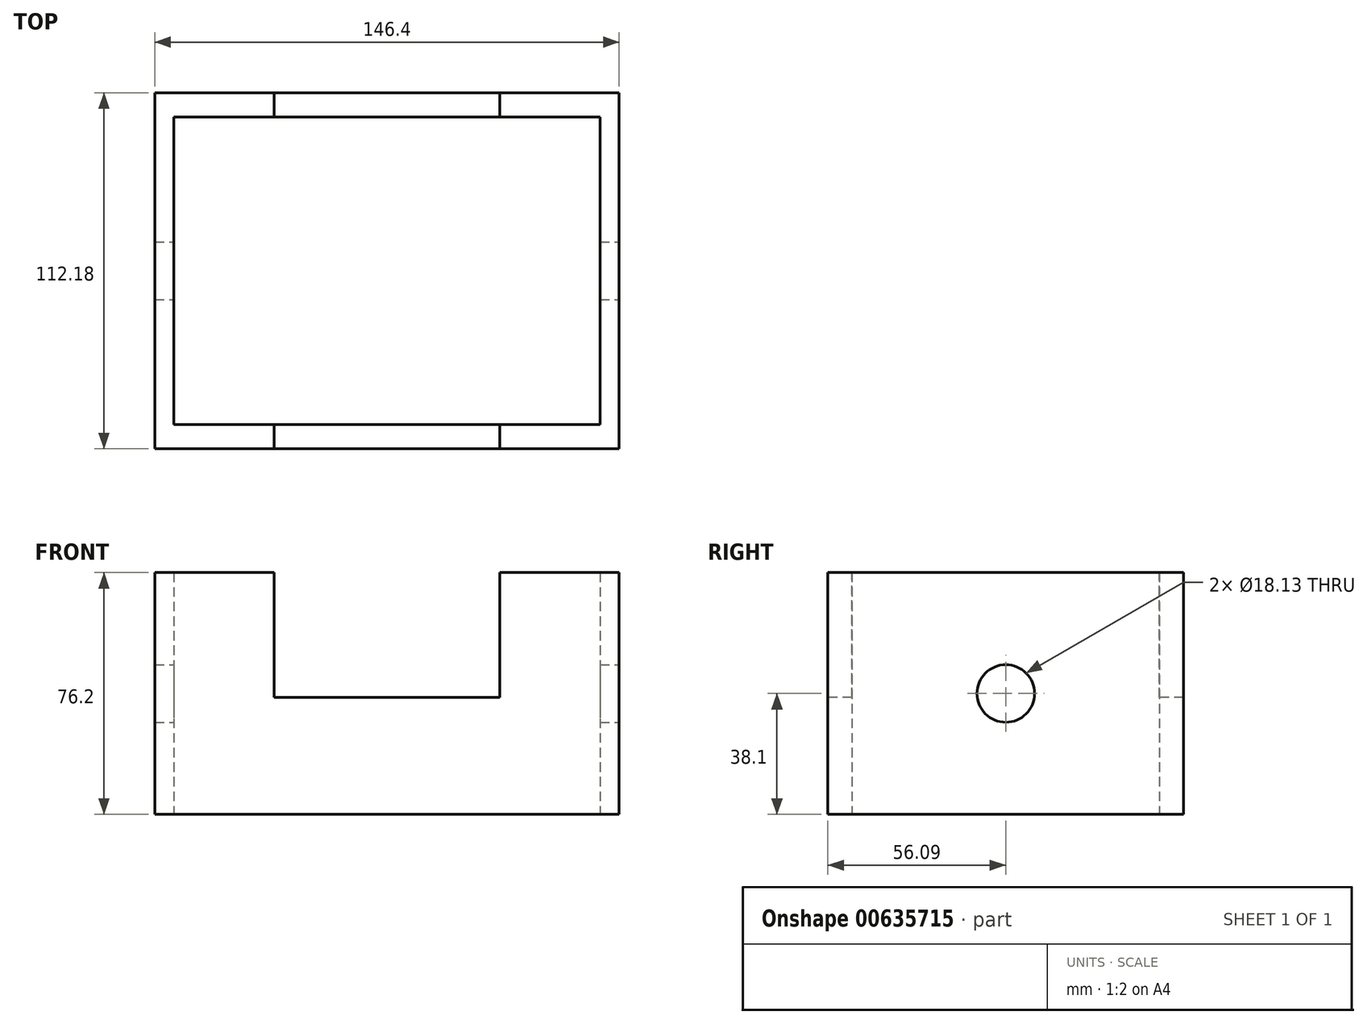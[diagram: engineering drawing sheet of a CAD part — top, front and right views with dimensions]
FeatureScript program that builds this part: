
annotation { "Feature Type Name" : "Feature", "Feature Type Description" : "" }
export const myFeature = defineFeature(function(context is Context, id is Id, definition is map)
    precondition{}
    {
        {
            var Q0;
            Q0=qCreatedBy(makeId("Top.planeOp"),FACE);
            var sketch = newSketch(context, id + "F0", { "sketchPlane" : qUnion([Q0])});
            skLineSegment(sketch, "E0.bottom", {"start": v(73.2, -56.1) * mm, "end": v(-73.2, -56.1) * mm});
            skLineSegment(sketch, "E0.top", {"start": v(73.2, 56.1) * mm, "end": v(-73.2, 56.1) * mm});
            skLineSegment(sketch, "E0.left", {"start": v(73.2, -56.1) * mm, "end": v(73.2, 56.1) * mm});
            skLineSegment(sketch, "E0.right", {"start": v(-73.2, -56.1) * mm, "end": v(-73.2, 56.1) * mm});
            skPoint(sketch, "E0.middle", {"position": v(0, 0) * mm});
            skLineSegment(sketch, "E1.bottom", {"start": v(67.15, -48.44) * mm, "end": v(-67.15, -48.44) * mm});
            skLineSegment(sketch, "E1.top", {"start": v(67.15, 48.44) * mm, "end": v(-67.15, 48.44) * mm});
            skLineSegment(sketch, "E1.left", {"start": v(67.15, -48.44) * mm, "end": v(67.15, 48.44) * mm});
            skLineSegment(sketch, "E1.right", {"start": v(-67.15, -48.44) * mm, "end": v(-67.15, 48.44) * mm});
            skSolve(sketch);
        }
        {
            var Q0;
            Q0=makeQuery(id+"F0.imprint","IMPRINT",FACE,{"disambiguationData":[TD([[makeQuery(id+"F0.imprint","IMPRINT",EDGE,{"derivedFrom":sQuery(id+"F0.wireOp",EDGE,"E0.bottom")}),-1.0]])]});
            extrude(context, id + "F1", {"entities" : qUnion([Q0]), "depth" : 76.2 * mm, "offsetDistance" : 25.4 * mm});
        }
        {
            var Q0;
            Q0=makeQuery(id+"F1.opExtrude","SWEPT_FACE",FACE,{"disambiguationData":[OSD([sQuery(id+"F0.wireOp",EDGE,"E0.bottom")])]});
            var sketch = newSketch(context, id + "F2", { "sketchPlane" : qUnion([Q0])});
            skLineSegment(sketch, "E2.bottom", {"start": v(35.5, 36.91) * mm, "end": v(-35.5, 36.91) * mm});
            skLineSegment(sketch, "E2.top", {"start": v(35.5, 115.49) * mm, "end": v(-35.5, 115.49) * mm});
            skLineSegment(sketch, "E2.left", {"start": v(35.5, 36.91) * mm, "end": v(35.5, 115.49) * mm});
            skLineSegment(sketch, "E2.right", {"start": v(-35.5, 36.91) * mm, "end": v(-35.5, 115.49) * mm});
            skPoint(sketch, "E2.middle", {"position": v(0, 76.2) * mm});
            skSolve(sketch);
        }
        {
            var Q0;
            {var subQ0=sQuery(id+"F2.wireOp",EDGE,"E2.top");Q0=makeQuery(id+"F2.imprint","IMPRINT",FACE,{"disambiguationData":[TD([[makeQuery(id+"F2.imprint","IMPRINT",EDGE,{"derivedFrom":subQ0}),1.0]])]});}
            var Q1;
            {var subQ0=sQuery(id+"F2.wireOp",EDGE,"E2.bottom");Q1=makeQuery(id+"F2.imprint","IMPRINT",FACE,{"disambiguationData":[TD([[makeQuery(id+"F2.imprint","IMPRINT",EDGE,{"derivedFrom":subQ0}),-1.0]])]});}
            extrude(context, id + "F3", {"entities" : qUnion([Q0, Q1]), "operationType" : NewBodyOperationType.REMOVE, "endBound" : BoundingType.THROUGH_ALL, "oppositeDirection" : true, "depth" : 25.4 * mm, "offsetDistance" : 25.4 * mm});
        }
        {
            var Q0;
            Q0=makeQuery(id+"F1.opExtrude","SWEPT_FACE",FACE,{"disambiguationData":[OSD([sQuery(id+"F0.wireOp",EDGE,"E0.left")])]});
            var sketch = newSketch(context, id + "F4", { "sketchPlane" : qUnion([Q0])});
            skCircle(sketch, "E3", {"center": v(0, 38.1) * mm, "radius": 9.07 * mm});
            skPoint(sketch, "E3.centerSnap0", {"position": v(56.1, 38.1) * mm});
            skPoint(sketch, "E3.centerSnap1", {"position": v(0, 76.2) * mm});
            skSolve(sketch);
        }
        {
            var Q0;
            Q0=makeQuery(id+"F4.imprint","IMPRINT",FACE,{"disambiguationData":[TD([[makeQuery(id+"F4.imprint","IMPRINT",EDGE,{"derivedFrom":sQuery(id+"F4.wireOp",EDGE,"E3")}),1.0]])]});
            extrude(context, id + "F5", {"entities" : qUnion([Q0]), "operationType" : NewBodyOperationType.REMOVE, "endBound" : BoundingType.THROUGH_ALL, "oppositeDirection" : true, "depth" : 25.4 * mm, "offsetDistance" : 25.4 * mm});
        }
    });
